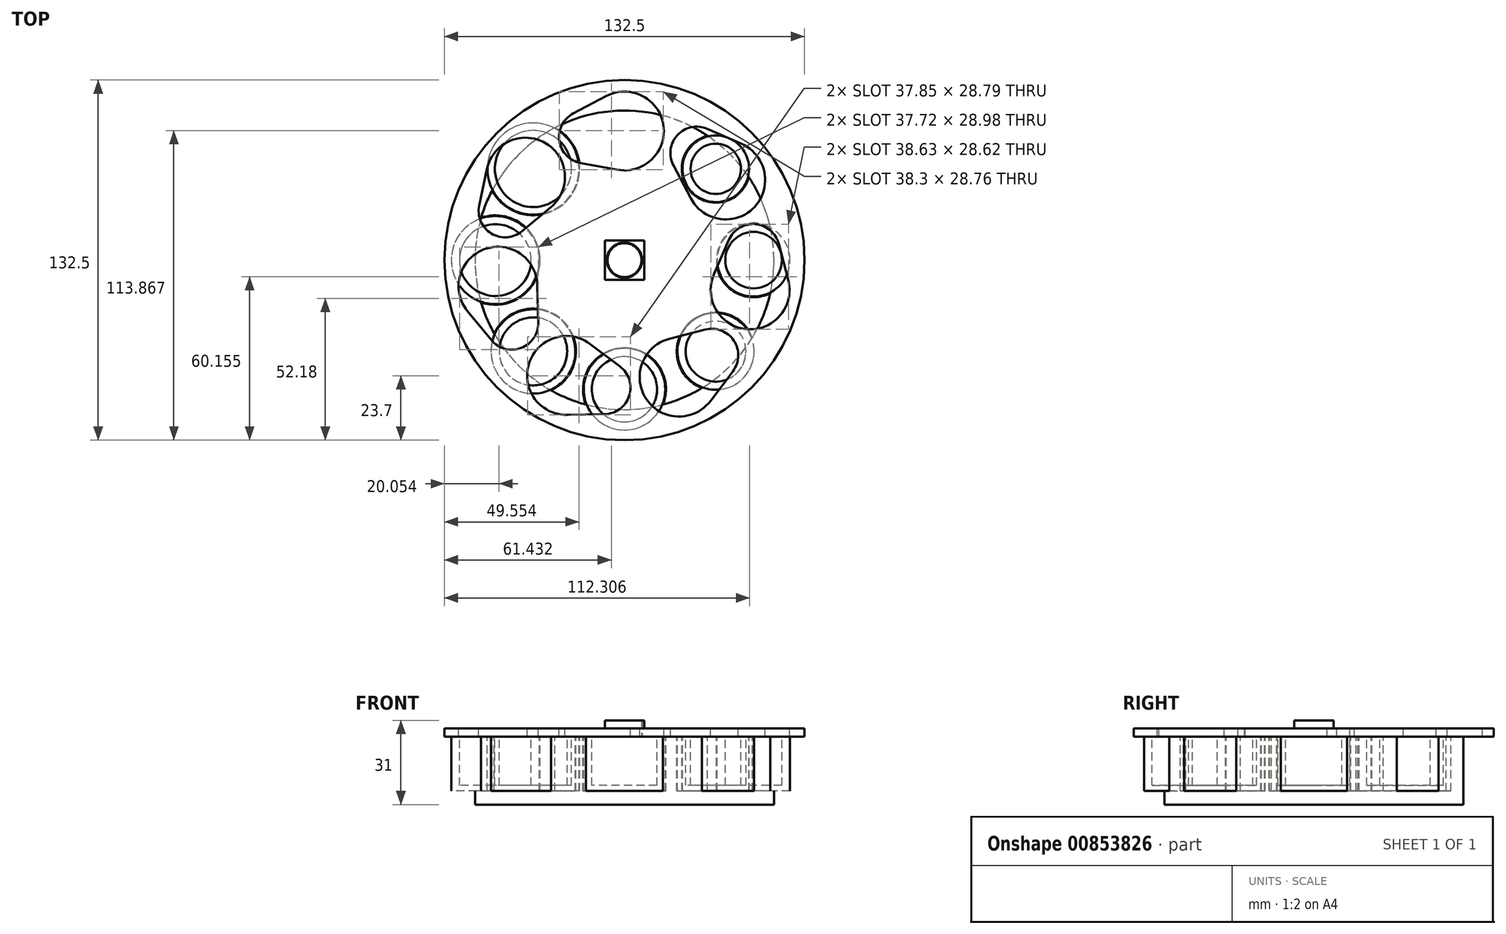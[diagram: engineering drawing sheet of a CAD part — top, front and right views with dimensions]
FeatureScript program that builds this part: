
annotation { "Feature Type Name" : "Feature", "Feature Type Description" : "" }
export const myFeature = defineFeature(function(context is Context, id is Id, definition is map)
    precondition{}
    {
        {
            var Q0;
            Q0=qCreatedBy(makeId("Top.planeOp"),FACE);
            var sketch = newSketch(context, id + "F0", { "sketchPlane" : qUnion([Q0])});
            skCircle(sketch, "E0", {"center": v(0, 0) * mm, "radius": 55 * mm});
            skCircle(sketch, "E1", {"center": v(0, 0) * mm, "radius": 47.5 * mm, "construction": true});
            skLineSegment(sketch, "E2", {"start": v(0, 0) * mm, "end": v(0, 47.5) * mm});
            skLineSegment(sketch, "E3.1.0", {"start": v(0, 0) * mm, "end": v(33.59, 33.59) * mm, "construction": true});
            skLineSegment(sketch, "E3.2.0", {"start": v(0, 0) * mm, "end": v(47.5, 0) * mm, "construction": true});
            skLineSegment(sketch, "E3.3.0", {"start": v(0, 0) * mm, "end": v(33.59, -33.59) * mm, "construction": true});
            skLineSegment(sketch, "E3.4.0", {"start": v(0, 0) * mm, "end": v(0, -47.5) * mm, "construction": true});
            skLineSegment(sketch, "E3.5.0", {"start": v(0, 0) * mm, "end": v(-33.59, -33.59) * mm, "construction": true});
            skLineSegment(sketch, "E3.6.0", {"start": v(0, 0) * mm, "end": v(-47.5, 0) * mm, "construction": true});
            skLineSegment(sketch, "E3.7.0", {"start": v(0, 0) * mm, "end": v(-33.59, 33.59) * mm});
            skLineSegment(sketch, "E3.anchor1", {"start": v(0, 0) * mm, "end": v(0, 47.5) * mm, "construction": true});
            skLineSegment(sketch, "E3.anchor2", {"start": v(0, 0) * mm, "end": v(-33.59, 33.59) * mm, "construction": true});
            skCircle(sketch, "E4", {"center": v(33.59, 33.59) * mm, "radius": 9.25 * mm});
            skCircle(sketch, "E5", {"center": v(47.5, 0) * mm, "radius": 10.4 * mm});
            skCircle(sketch, "E6", {"center": v(33.59, -33.59) * mm, "radius": 11.1 * mm});
            skCircle(sketch, "E7", {"center": v(0, -47.5) * mm, "radius": 12 * mm});
            skCircle(sketch, "E8", {"center": v(-33.59, -33.59) * mm, "radius": 12.5 * mm});
            skCircle(sketch, "E9", {"center": v(-47.5, 0) * mm, "radius": 13.2 * mm});
            skCircle(sketch, "E10", {"center": v(-33.59, 33.59) * mm, "radius": 14.1 * mm});
            skCircle(sketch, "E11.0", {"center": v(33.59, 33.59) * mm, "radius": 12.25 * mm});
            skCircle(sketch, "E12.0", {"center": v(47.5, 0) * mm, "radius": 13.4 * mm});
            skCircle(sketch, "E13.0", {"center": v(33.59, -33.59) * mm, "radius": 14.1 * mm});
            skCircle(sketch, "E14.0", {"center": v(0, -47.5) * mm, "radius": 15 * mm});
            skCircle(sketch, "E15.0", {"center": v(-33.59, -33.59) * mm, "radius": 15.5 * mm});
            skArc(sketch, "E16.0", {"start": v(-48.7, 25.57) * mm, "mid": v(-21.5, 21.5) * mm, "end": v(-25.57, 48.7) * mm});
            skArc(sketch, "E17.0", {"start": v(30.57, 45.72) * mm, "mid": v(24.75, 24.75) * mm, "end": v(45.72, 30.57) * mm});
            skArc(sketch, "E18.0", {"start": v(53.63, 12.2) * mm, "mid": v(33.85, 0) * mm, "end": v(53.63, -12.2) * mm});
            skArc(sketch, "E19.0", {"start": v(47.02, -28.53) * mm, "mid": v(23.44, -23.44) * mm, "end": v(28.53, -47.02) * mm});
            skArc(sketch, "E20.0", {"start": v(14.17, -53.14) * mm, "mid": v(0, -32.25) * mm, "end": v(-14.17, -53.14) * mm});
            skArc(sketch, "E21.0", {"start": v(-27.02, -47.9) * mm, "mid": v(-22.45, -22.45) * mm, "end": v(-47.9, -27.02) * mm});
            skCircle(sketch, "E22.0", {"center": v(-33.59, 33.59) * mm, "radius": 16.85 * mm});
            skCircle(sketch, "E23.0", {"center": v(-47.5, 0) * mm, "radius": 16.2 * mm});
            skArc(sketch, "E24.0", {"start": v(-52.74, -15.6) * mm, "mid": v(-31.05, 0) * mm, "end": v(-52.74, 15.6) * mm});
            skSolve(sketch);
        }
        {
            var Q0;
            {var subQ0=sQuery(id+"F0.wireOp",EDGE,"E16.0");var subQ1=sQuery(id+"F0.wireOp",EDGE,"E0");var subQ2=makeQuery(id+"F0.imprint","INTERSECT",VERTEX,{"disambiguationData":[OD(1.0)],"derivedFrom":[subQ1,subQ0]});Q0=makeQuery(id+"F0.imprint","IMPRINT",FACE,{"disambiguationData":[TD([[makeQuery(id+"F0.imprint","IMPRINT",EDGE,{"disambiguationData":[TD([[subQ2,1.0]])],"derivedFrom":subQ1}),1.0]])]});}
            var Q1;
            {var subQ5=sQuery(id+"F0.wireOp",EDGE,"E17.0");var subQ6=sQuery(id+"F0.wireOp",EDGE,"E0");var subQ7=makeQuery(id+"F0.imprint","INTERSECT",VERTEX,{"disambiguationData":[OD(1.0)],"derivedFrom":[subQ6,subQ5]});Q1=makeQuery(id+"F0.imprint","IMPRINT",FACE,{"disambiguationData":[TD([[makeQuery(id+"F0.imprint","IMPRINT",EDGE,{"disambiguationData":[TD([[subQ7,1.0]])],"derivedFrom":subQ6}),1.0]])]});}
            var Q2;
            {var subQ0=sQuery(id+"F0.wireOp",EDGE,"E18.0");var subQ1=sQuery(id+"F0.wireOp",EDGE,"E0");var subQ2=makeQuery(id+"F0.imprint","INTERSECT",VERTEX,{"disambiguationData":[OD(1.0)],"derivedFrom":[subQ1,subQ0]});Q2=makeQuery(id+"F0.imprint","IMPRINT",FACE,{"disambiguationData":[TD([[makeQuery(id+"F0.imprint","IMPRINT",EDGE,{"disambiguationData":[TD([[subQ2,1.0]])],"derivedFrom":subQ1}),1.0]])]});}
            var Q3;
            {var subQ0=sQuery(id+"F0.wireOp",EDGE,"E19.0");var subQ1=sQuery(id+"F0.wireOp",EDGE,"E0");var subQ2=makeQuery(id+"F0.imprint","INTERSECT",VERTEX,{"disambiguationData":[OD(1.0)],"derivedFrom":[subQ1,subQ0]});Q3=makeQuery(id+"F0.imprint","IMPRINT",FACE,{"disambiguationData":[TD([[makeQuery(id+"F0.imprint","IMPRINT",EDGE,{"disambiguationData":[TD([[subQ2,1.0]])],"derivedFrom":subQ1}),1.0]])]});}
            var Q4;
            {var subQ0=sQuery(id+"F0.wireOp",EDGE,"E20.0");var subQ1=sQuery(id+"F0.wireOp",EDGE,"E0");var subQ2=makeQuery(id+"F0.imprint","INTERSECT",VERTEX,{"disambiguationData":[OD(1.0)],"derivedFrom":[subQ1,subQ0]});Q4=makeQuery(id+"F0.imprint","IMPRINT",FACE,{"disambiguationData":[TD([[makeQuery(id+"F0.imprint","IMPRINT",EDGE,{"disambiguationData":[TD([[subQ2,1.0]])],"derivedFrom":subQ1}),1.0]])]});}
            var Q5;
            {var subQ5=sQuery(id+"F0.wireOp",EDGE,"E21.0");var subQ7=sQuery(id+"F0.wireOp",EDGE,"E0");var subQ8=makeQuery(id+"F0.imprint","INTERSECT",VERTEX,{"disambiguationData":[OD(1.0)],"derivedFrom":[subQ7,subQ5]});Q5=makeQuery(id+"F0.imprint","IMPRINT",FACE,{"disambiguationData":[TD([[makeQuery(id+"F0.imprint","IMPRINT",EDGE,{"disambiguationData":[TD([[subQ8,1.0]])],"derivedFrom":subQ7}),1.0]])]});}
            var Q6;
            {var subQ3=sQuery(id+"F0.wireOp",EDGE,"E16.0");var subQ7=sQuery(id+"F0.wireOp",EDGE,"E0");var subQ8=makeQuery(id+"F0.imprint","INTERSECT",VERTEX,{"disambiguationData":[OD(0.0)],"derivedFrom":[subQ7,subQ3]});Q6=makeQuery(id+"F0.imprint","IMPRINT",FACE,{"disambiguationData":[TD([[makeQuery(id+"F0.imprint","IMPRINT",EDGE,{"disambiguationData":[TD([[subQ8,-1.0]])],"derivedFrom":subQ7}),1.0]])]});}
            extrude(context, id + "F1", {"entities" : qUnion([Q0, Q1, Q2, Q3, Q4, Q5, Q6]), "oppositeDirection" : true, "depth" : 20 * mm, "offsetDistance" : 25 * mm});
        }
        {
            var Q0;
            {var subQ0=sQuery(id+"F0.wireOp",EDGE,"E16.0");var subQ1=sQuery(id+"F0.wireOp",EDGE,"E0");var subQ2=makeQuery(id+"F0.imprint","INTERSECT",VERTEX,{"disambiguationData":[OD(1.0)],"derivedFrom":[subQ1,subQ0]});Q0=makeQuery(id+"F0.imprint","IMPRINT",FACE,{"disambiguationData":[TD([[makeQuery(id+"F0.imprint","IMPRINT",EDGE,{"disambiguationData":[TD([[subQ2,1.0]])],"derivedFrom":subQ1}),1.0]])]});}
            var Q1;
            {var subQ5=sQuery(id+"F0.wireOp",EDGE,"E17.0");var subQ6=sQuery(id+"F0.wireOp",EDGE,"E0");var subQ7=makeQuery(id+"F0.imprint","INTERSECT",VERTEX,{"disambiguationData":[OD(1.0)],"derivedFrom":[subQ6,subQ5]});Q1=makeQuery(id+"F0.imprint","IMPRINT",FACE,{"disambiguationData":[TD([[makeQuery(id+"F0.imprint","IMPRINT",EDGE,{"disambiguationData":[TD([[subQ7,1.0]])],"derivedFrom":subQ6}),1.0]])]});}
            var Q2;
            {var subQ0=sQuery(id+"F0.wireOp",EDGE,"E18.0");var subQ1=sQuery(id+"F0.wireOp",EDGE,"E0");var subQ2=makeQuery(id+"F0.imprint","INTERSECT",VERTEX,{"disambiguationData":[OD(1.0)],"derivedFrom":[subQ1,subQ0]});Q2=makeQuery(id+"F0.imprint","IMPRINT",FACE,{"disambiguationData":[TD([[makeQuery(id+"F0.imprint","IMPRINT",EDGE,{"disambiguationData":[TD([[subQ2,1.0]])],"derivedFrom":subQ1}),1.0]])]});}
            var Q3;
            {var subQ0=sQuery(id+"F0.wireOp",EDGE,"E19.0");var subQ1=sQuery(id+"F0.wireOp",EDGE,"E0");var subQ2=makeQuery(id+"F0.imprint","INTERSECT",VERTEX,{"disambiguationData":[OD(1.0)],"derivedFrom":[subQ1,subQ0]});Q3=makeQuery(id+"F0.imprint","IMPRINT",FACE,{"disambiguationData":[TD([[makeQuery(id+"F0.imprint","IMPRINT",EDGE,{"disambiguationData":[TD([[subQ2,1.0]])],"derivedFrom":subQ1}),1.0]])]});}
            var Q4;
            {var subQ0=sQuery(id+"F0.wireOp",EDGE,"E20.0");var subQ1=sQuery(id+"F0.wireOp",EDGE,"E0");var subQ2=makeQuery(id+"F0.imprint","INTERSECT",VERTEX,{"disambiguationData":[OD(1.0)],"derivedFrom":[subQ1,subQ0]});Q4=makeQuery(id+"F0.imprint","IMPRINT",FACE,{"disambiguationData":[TD([[makeQuery(id+"F0.imprint","IMPRINT",EDGE,{"disambiguationData":[TD([[subQ2,1.0]])],"derivedFrom":subQ1}),1.0]])]});}
            var Q5;
            {var subQ5=sQuery(id+"F0.wireOp",EDGE,"E21.0");var subQ7=sQuery(id+"F0.wireOp",EDGE,"E0");var subQ8=makeQuery(id+"F0.imprint","INTERSECT",VERTEX,{"disambiguationData":[OD(1.0)],"derivedFrom":[subQ7,subQ5]});Q5=makeQuery(id+"F0.imprint","IMPRINT",FACE,{"disambiguationData":[TD([[makeQuery(id+"F0.imprint","IMPRINT",EDGE,{"disambiguationData":[TD([[subQ8,1.0]])],"derivedFrom":subQ7}),1.0]])]});}
            var Q6;
            {var subQ3=sQuery(id+"F0.wireOp",EDGE,"E16.0");var subQ7=sQuery(id+"F0.wireOp",EDGE,"E0");var subQ8=makeQuery(id+"F0.imprint","INTERSECT",VERTEX,{"disambiguationData":[OD(0.0)],"derivedFrom":[subQ7,subQ3]});Q6=makeQuery(id+"F0.imprint","IMPRINT",FACE,{"disambiguationData":[TD([[makeQuery(id+"F0.imprint","IMPRINT",EDGE,{"disambiguationData":[TD([[subQ8,-1.0]])],"derivedFrom":subQ7}),1.0]])]});}
            var Q7;
            {var subQ0=sQuery(id+"F0.wireOp",EDGE,"E22.0");var subQ1=sQuery(id+"F0.wireOp",EDGE,"E0");var subQ2=makeQuery(id+"F0.imprint","INTERSECT",VERTEX,{"disambiguationData":[OD(1.0)],"derivedFrom":[subQ1,subQ0]});Q7=makeQuery(id+"F0.imprint","IMPRINT",FACE,{"disambiguationData":[TD([[makeQuery(id+"F0.imprint","IMPRINT",EDGE,{"disambiguationData":[TD([[subQ2,1.0]])],"derivedFrom":subQ1}),1.0]])]});}
            var Q8;
            {var subQ0=sQuery(id+"F0.wireOp",EDGE,"E10");var subQ1=sQuery(id+"F0.wireOp",EDGE,"E0");var subQ2=makeQuery(id+"F0.imprint","INTERSECT",VERTEX,{"disambiguationData":[OD(0.0)],"derivedFrom":[subQ1,subQ0]});Q8=makeQuery(id+"F0.imprint","IMPRINT",FACE,{"disambiguationData":[TD([[makeQuery(id+"F0.imprint","IMPRINT",EDGE,{"disambiguationData":[TD([[subQ2,-1.0]])],"derivedFrom":subQ1}),1.0]])]});}
            var Q9;
            {var subQ0=sQuery(id+"F0.wireOp",EDGE,"E22.0");var subQ1=sQuery(id+"F0.wireOp",EDGE,"E0");var subQ2=makeQuery(id+"F0.imprint","INTERSECT",VERTEX,{"disambiguationData":[OD(0.0)],"derivedFrom":[subQ1,subQ0]});Q9=makeQuery(id+"F0.imprint","IMPRINT",FACE,{"disambiguationData":[TD([[makeQuery(id+"F0.imprint","IMPRINT",EDGE,{"disambiguationData":[TD([[subQ2,-1.0]])],"derivedFrom":subQ1}),1.0]])]});}
            var Q10;
            {var subQ0=sQuery(id+"F0.wireOp",EDGE,"E11.0");var subQ1=sQuery(id+"F0.wireOp",EDGE,"E0");var subQ2=makeQuery(id+"F0.imprint","INTERSECT",VERTEX,{"disambiguationData":[OD(1.0)],"derivedFrom":[subQ1,subQ0]});Q10=makeQuery(id+"F0.imprint","IMPRINT",FACE,{"disambiguationData":[TD([[makeQuery(id+"F0.imprint","IMPRINT",EDGE,{"disambiguationData":[TD([[subQ2,1.0]])],"derivedFrom":subQ1}),1.0]])]});}
            var Q11;
            {var subQ0=sQuery(id+"F0.wireOp",EDGE,"E4");var subQ1=sQuery(id+"F0.wireOp",EDGE,"E0");var subQ2=makeQuery(id+"F0.imprint","INTERSECT",VERTEX,{"disambiguationData":[OD(0.0)],"derivedFrom":[subQ1,subQ0]});Q11=makeQuery(id+"F0.imprint","IMPRINT",FACE,{"disambiguationData":[TD([[makeQuery(id+"F0.imprint","IMPRINT",EDGE,{"disambiguationData":[TD([[subQ2,-1.0]])],"derivedFrom":subQ1}),1.0]])]});}
            var Q12;
            {var subQ0=sQuery(id+"F0.wireOp",EDGE,"E11.0");var subQ1=sQuery(id+"F0.wireOp",EDGE,"E0");var subQ2=makeQuery(id+"F0.imprint","INTERSECT",VERTEX,{"disambiguationData":[OD(0.0)],"derivedFrom":[subQ1,subQ0]});Q12=makeQuery(id+"F0.imprint","IMPRINT",FACE,{"disambiguationData":[TD([[makeQuery(id+"F0.imprint","IMPRINT",EDGE,{"disambiguationData":[TD([[subQ2,-1.0]])],"derivedFrom":subQ1}),1.0]])]});}
            var Q13;
            {var subQ0=sQuery(id+"F0.wireOp",EDGE,"E12.0");var subQ1=sQuery(id+"F0.wireOp",EDGE,"E0");var subQ2=makeQuery(id+"F0.imprint","INTERSECT",VERTEX,{"disambiguationData":[OD(0.0)],"derivedFrom":[subQ1,subQ0]});Q13=makeQuery(id+"F0.imprint","IMPRINT",FACE,{"disambiguationData":[TD([[makeQuery(id+"F0.imprint","IMPRINT",EDGE,{"disambiguationData":[TD([[subQ2,1.0]])],"derivedFrom":subQ1}),1.0]])]});}
            var Q14;
            {var subQ0=sQuery(id+"F0.wireOp",EDGE,"E5");var subQ1=sQuery(id+"F0.wireOp",EDGE,"E0");var subQ2=makeQuery(id+"F0.imprint","INTERSECT",VERTEX,{"disambiguationData":[OD(0.0)],"derivedFrom":[subQ1,subQ0]});Q14=makeQuery(id+"F0.imprint","IMPRINT",FACE,{"disambiguationData":[TD([[makeQuery(id+"F0.imprint","IMPRINT",EDGE,{"disambiguationData":[TD([[subQ2,1.0]])],"derivedFrom":subQ1}),1.0]])]});}
            var Q15;
            {var subQ0=sQuery(id+"F0.wireOp",EDGE,"E12.0");var subQ1=sQuery(id+"F0.wireOp",EDGE,"E0");var subQ2=makeQuery(id+"F0.imprint","INTERSECT",VERTEX,{"disambiguationData":[OD(1.0)],"derivedFrom":[subQ1,subQ0]});Q15=makeQuery(id+"F0.imprint","IMPRINT",FACE,{"disambiguationData":[TD([[makeQuery(id+"F0.imprint","IMPRINT",EDGE,{"disambiguationData":[TD([[subQ2,-1.0]])],"derivedFrom":subQ1}),1.0]])]});}
            var Q16;
            {var subQ0=sQuery(id+"F0.wireOp",EDGE,"E13.0");var subQ1=sQuery(id+"F0.wireOp",EDGE,"E0");var subQ2=makeQuery(id+"F0.imprint","INTERSECT",VERTEX,{"disambiguationData":[OD(1.0)],"derivedFrom":[subQ1,subQ0]});Q16=makeQuery(id+"F0.imprint","IMPRINT",FACE,{"disambiguationData":[TD([[makeQuery(id+"F0.imprint","IMPRINT",EDGE,{"disambiguationData":[TD([[subQ2,1.0]])],"derivedFrom":subQ1}),1.0]])]});}
            var Q17;
            {var subQ0=sQuery(id+"F0.wireOp",EDGE,"E6");var subQ1=sQuery(id+"F0.wireOp",EDGE,"E0");var subQ2=makeQuery(id+"F0.imprint","INTERSECT",VERTEX,{"disambiguationData":[OD(0.0)],"derivedFrom":[subQ1,subQ0]});Q17=makeQuery(id+"F0.imprint","IMPRINT",FACE,{"disambiguationData":[TD([[makeQuery(id+"F0.imprint","IMPRINT",EDGE,{"disambiguationData":[TD([[subQ2,-1.0]])],"derivedFrom":subQ1}),1.0]])]});}
            var Q18;
            {var subQ0=sQuery(id+"F0.wireOp",EDGE,"E13.0");var subQ1=sQuery(id+"F0.wireOp",EDGE,"E0");var subQ2=makeQuery(id+"F0.imprint","INTERSECT",VERTEX,{"disambiguationData":[OD(0.0)],"derivedFrom":[subQ1,subQ0]});Q18=makeQuery(id+"F0.imprint","IMPRINT",FACE,{"disambiguationData":[TD([[makeQuery(id+"F0.imprint","IMPRINT",EDGE,{"disambiguationData":[TD([[subQ2,-1.0]])],"derivedFrom":subQ1}),1.0]])]});}
            var Q19;
            {var subQ0=sQuery(id+"F0.wireOp",EDGE,"E14.0");var subQ1=sQuery(id+"F0.wireOp",EDGE,"E0");var subQ2=makeQuery(id+"F0.imprint","INTERSECT",VERTEX,{"disambiguationData":[OD(1.0)],"derivedFrom":[subQ1,subQ0]});Q19=makeQuery(id+"F0.imprint","IMPRINT",FACE,{"disambiguationData":[TD([[makeQuery(id+"F0.imprint","IMPRINT",EDGE,{"disambiguationData":[TD([[subQ2,1.0]])],"derivedFrom":subQ1}),1.0]])]});}
            var Q20;
            {var subQ0=sQuery(id+"F0.wireOp",EDGE,"E7");var subQ1=sQuery(id+"F0.wireOp",EDGE,"E0");var subQ2=makeQuery(id+"F0.imprint","INTERSECT",VERTEX,{"disambiguationData":[OD(0.0)],"derivedFrom":[subQ1,subQ0]});Q20=makeQuery(id+"F0.imprint","IMPRINT",FACE,{"disambiguationData":[TD([[makeQuery(id+"F0.imprint","IMPRINT",EDGE,{"disambiguationData":[TD([[subQ2,-1.0]])],"derivedFrom":subQ1}),1.0]])]});}
            var Q21;
            {var subQ0=sQuery(id+"F0.wireOp",EDGE,"E14.0");var subQ1=sQuery(id+"F0.wireOp",EDGE,"E0");var subQ2=makeQuery(id+"F0.imprint","INTERSECT",VERTEX,{"disambiguationData":[OD(0.0)],"derivedFrom":[subQ1,subQ0]});Q21=makeQuery(id+"F0.imprint","IMPRINT",FACE,{"disambiguationData":[TD([[makeQuery(id+"F0.imprint","IMPRINT",EDGE,{"disambiguationData":[TD([[subQ2,-1.0]])],"derivedFrom":subQ1}),1.0]])]});}
            var Q22;
            {var subQ0=sQuery(id+"F0.wireOp",EDGE,"E15.0");var subQ1=sQuery(id+"F0.wireOp",EDGE,"E0");var subQ2=makeQuery(id+"F0.imprint","INTERSECT",VERTEX,{"disambiguationData":[OD(1.0)],"derivedFrom":[subQ1,subQ0]});Q22=makeQuery(id+"F0.imprint","IMPRINT",FACE,{"disambiguationData":[TD([[makeQuery(id+"F0.imprint","IMPRINT",EDGE,{"disambiguationData":[TD([[subQ2,1.0]])],"derivedFrom":subQ1}),1.0]])]});}
            var Q23;
            {var subQ0=sQuery(id+"F0.wireOp",EDGE,"E8");var subQ1=sQuery(id+"F0.wireOp",EDGE,"E0");var subQ2=makeQuery(id+"F0.imprint","INTERSECT",VERTEX,{"disambiguationData":[OD(0.0)],"derivedFrom":[subQ1,subQ0]});Q23=makeQuery(id+"F0.imprint","IMPRINT",FACE,{"disambiguationData":[TD([[makeQuery(id+"F0.imprint","IMPRINT",EDGE,{"disambiguationData":[TD([[subQ2,-1.0]])],"derivedFrom":subQ1}),1.0]])]});}
            var Q24;
            {var subQ0=sQuery(id+"F0.wireOp",EDGE,"E15.0");var subQ1=sQuery(id+"F0.wireOp",EDGE,"E0");var subQ2=makeQuery(id+"F0.imprint","INTERSECT",VERTEX,{"disambiguationData":[OD(0.0)],"derivedFrom":[subQ1,subQ0]});Q24=makeQuery(id+"F0.imprint","IMPRINT",FACE,{"disambiguationData":[TD([[makeQuery(id+"F0.imprint","IMPRINT",EDGE,{"disambiguationData":[TD([[subQ2,-1.0]])],"derivedFrom":subQ1}),1.0]])]});}
            var Q25;
            {var subQ0=sQuery(id+"F0.wireOp",EDGE,"E23.0");var subQ1=sQuery(id+"F0.wireOp",EDGE,"E0");var subQ2=makeQuery(id+"F0.imprint","INTERSECT",VERTEX,{"disambiguationData":[OD(1.0)],"derivedFrom":[subQ1,subQ0]});Q25=makeQuery(id+"F0.imprint","IMPRINT",FACE,{"disambiguationData":[TD([[makeQuery(id+"F0.imprint","IMPRINT",EDGE,{"disambiguationData":[TD([[subQ2,1.0]])],"derivedFrom":subQ1}),1.0]])]});}
            var Q26;
            {var subQ0=sQuery(id+"F0.wireOp",EDGE,"E9");var subQ1=sQuery(id+"F0.wireOp",EDGE,"E0");var subQ2=makeQuery(id+"F0.imprint","INTERSECT",VERTEX,{"disambiguationData":[OD(0.0)],"derivedFrom":[subQ1,subQ0]});Q26=makeQuery(id+"F0.imprint","IMPRINT",FACE,{"disambiguationData":[TD([[makeQuery(id+"F0.imprint","IMPRINT",EDGE,{"disambiguationData":[TD([[subQ2,-1.0]])],"derivedFrom":subQ1}),1.0]])]});}
            var Q27;
            {var subQ0=sQuery(id+"F0.wireOp",EDGE,"E23.0");var subQ1=sQuery(id+"F0.wireOp",EDGE,"E0");var subQ2=makeQuery(id+"F0.imprint","INTERSECT",VERTEX,{"disambiguationData":[OD(0.0)],"derivedFrom":[subQ1,subQ0]});Q27=makeQuery(id+"F0.imprint","IMPRINT",FACE,{"disambiguationData":[TD([[makeQuery(id+"F0.imprint","IMPRINT",EDGE,{"disambiguationData":[TD([[subQ2,-1.0]])],"derivedFrom":subQ1}),1.0]])]});}
            var Q28;
            {var subQ0=sQuery(id+"F0.wireOp",EDGE,"E16.0");var subQ1=sQuery(id+"F0.wireOp",EDGE,"E0");var subQ2=makeQuery(id+"F0.imprint","INTERSECT",VERTEX,{"disambiguationData":[OD(0.0)],"derivedFrom":[subQ1,subQ0]});Q28=makeQuery(id+"F0.imprint","IMPRINT",FACE,{"disambiguationData":[TD([[makeQuery(id+"F0.imprint","IMPRINT",EDGE,{"disambiguationData":[TD([[subQ2,1.0]])],"derivedFrom":subQ1}),1.0]])]});}
            var Q29;
            {var subQ0=sQuery(id+"F0.wireOp",EDGE,"E16.0");var subQ1=sQuery(id+"F0.wireOp",EDGE,"E0");var subQ2=makeQuery(id+"F0.imprint","INTERSECT",VERTEX,{"disambiguationData":[OD(1.0)],"derivedFrom":[subQ1,subQ0]});Q29=makeQuery(id+"F0.imprint","IMPRINT",FACE,{"disambiguationData":[TD([[makeQuery(id+"F0.imprint","IMPRINT",EDGE,{"disambiguationData":[TD([[subQ2,-1.0]])],"derivedFrom":subQ1}),1.0]])]});}
            var Q30;
            {var subQ0=sQuery(id+"F0.wireOp",EDGE,"E17.0");var subQ1=sQuery(id+"F0.wireOp",EDGE,"E0");var subQ2=makeQuery(id+"F0.imprint","INTERSECT",VERTEX,{"disambiguationData":[OD(1.0)],"derivedFrom":[subQ1,subQ0]});Q30=makeQuery(id+"F0.imprint","IMPRINT",FACE,{"disambiguationData":[TD([[makeQuery(id+"F0.imprint","IMPRINT",EDGE,{"disambiguationData":[TD([[subQ2,-1.0]])],"derivedFrom":subQ1}),1.0]])]});}
            var Q31;
            {var subQ0=sQuery(id+"F0.wireOp",EDGE,"E17.0");var subQ1=sQuery(id+"F0.wireOp",EDGE,"E0");var subQ2=makeQuery(id+"F0.imprint","INTERSECT",VERTEX,{"disambiguationData":[OD(0.0)],"derivedFrom":[subQ1,subQ0]});Q31=makeQuery(id+"F0.imprint","IMPRINT",FACE,{"disambiguationData":[TD([[makeQuery(id+"F0.imprint","IMPRINT",EDGE,{"disambiguationData":[TD([[subQ2,1.0]])],"derivedFrom":subQ1}),1.0]])]});}
            var Q32;
            {var subQ0=sQuery(id+"F0.wireOp",EDGE,"E18.0");var subQ1=sQuery(id+"F0.wireOp",EDGE,"E0");var subQ2=makeQuery(id+"F0.imprint","INTERSECT",VERTEX,{"disambiguationData":[OD(0.0)],"derivedFrom":[subQ1,subQ0]});Q32=makeQuery(id+"F0.imprint","IMPRINT",FACE,{"disambiguationData":[TD([[makeQuery(id+"F0.imprint","IMPRINT",EDGE,{"disambiguationData":[TD([[subQ2,1.0]])],"derivedFrom":subQ1}),1.0]])]});}
            var Q33;
            {var subQ0=sQuery(id+"F0.wireOp",EDGE,"E18.0");var subQ1=sQuery(id+"F0.wireOp",EDGE,"E0");var subQ2=makeQuery(id+"F0.imprint","INTERSECT",VERTEX,{"disambiguationData":[OD(1.0)],"derivedFrom":[subQ1,subQ0]});Q33=makeQuery(id+"F0.imprint","IMPRINT",FACE,{"disambiguationData":[TD([[makeQuery(id+"F0.imprint","IMPRINT",EDGE,{"disambiguationData":[TD([[subQ2,-1.0]])],"derivedFrom":subQ1}),1.0]])]});}
            var Q34;
            {var subQ0=sQuery(id+"F0.wireOp",EDGE,"E19.0");var subQ1=sQuery(id+"F0.wireOp",EDGE,"E0");var subQ2=makeQuery(id+"F0.imprint","INTERSECT",VERTEX,{"disambiguationData":[OD(0.0)],"derivedFrom":[subQ1,subQ0]});Q34=makeQuery(id+"F0.imprint","IMPRINT",FACE,{"disambiguationData":[TD([[makeQuery(id+"F0.imprint","IMPRINT",EDGE,{"disambiguationData":[TD([[subQ2,1.0]])],"derivedFrom":subQ1}),1.0]])]});}
            var Q35;
            {var subQ0=sQuery(id+"F0.wireOp",EDGE,"E19.0");var subQ1=sQuery(id+"F0.wireOp",EDGE,"E0");var subQ2=makeQuery(id+"F0.imprint","INTERSECT",VERTEX,{"disambiguationData":[OD(1.0)],"derivedFrom":[subQ1,subQ0]});Q35=makeQuery(id+"F0.imprint","IMPRINT",FACE,{"disambiguationData":[TD([[makeQuery(id+"F0.imprint","IMPRINT",EDGE,{"disambiguationData":[TD([[subQ2,-1.0]])],"derivedFrom":subQ1}),1.0]])]});}
            var Q36;
            {var subQ0=sQuery(id+"F0.wireOp",EDGE,"E20.0");var subQ1=sQuery(id+"F0.wireOp",EDGE,"E0");var subQ2=makeQuery(id+"F0.imprint","INTERSECT",VERTEX,{"disambiguationData":[OD(0.0)],"derivedFrom":[subQ1,subQ0]});Q36=makeQuery(id+"F0.imprint","IMPRINT",FACE,{"disambiguationData":[TD([[makeQuery(id+"F0.imprint","IMPRINT",EDGE,{"disambiguationData":[TD([[subQ2,1.0]])],"derivedFrom":subQ1}),1.0]])]});}
            var Q37;
            {var subQ0=sQuery(id+"F0.wireOp",EDGE,"E20.0");var subQ1=sQuery(id+"F0.wireOp",EDGE,"E0");var subQ2=makeQuery(id+"F0.imprint","INTERSECT",VERTEX,{"disambiguationData":[OD(1.0)],"derivedFrom":[subQ1,subQ0]});Q37=makeQuery(id+"F0.imprint","IMPRINT",FACE,{"disambiguationData":[TD([[makeQuery(id+"F0.imprint","IMPRINT",EDGE,{"disambiguationData":[TD([[subQ2,-1.0]])],"derivedFrom":subQ1}),1.0]])]});}
            var Q38;
            {var subQ0=sQuery(id+"F0.wireOp",EDGE,"E21.0");var subQ1=sQuery(id+"F0.wireOp",EDGE,"E0");var subQ2=makeQuery(id+"F0.imprint","INTERSECT",VERTEX,{"disambiguationData":[OD(0.0)],"derivedFrom":[subQ1,subQ0]});Q38=makeQuery(id+"F0.imprint","IMPRINT",FACE,{"disambiguationData":[TD([[makeQuery(id+"F0.imprint","IMPRINT",EDGE,{"disambiguationData":[TD([[subQ2,1.0]])],"derivedFrom":subQ1}),1.0]])]});}
            var Q39;
            {var subQ0=sQuery(id+"F0.wireOp",EDGE,"E21.0");var subQ1=sQuery(id+"F0.wireOp",EDGE,"E0");var subQ2=makeQuery(id+"F0.imprint","INTERSECT",VERTEX,{"disambiguationData":[OD(1.0)],"derivedFrom":[subQ1,subQ0]});Q39=makeQuery(id+"F0.imprint","IMPRINT",FACE,{"disambiguationData":[TD([[makeQuery(id+"F0.imprint","IMPRINT",EDGE,{"disambiguationData":[TD([[subQ2,-1.0]])],"derivedFrom":subQ1}),1.0]])]});}
            var Q40;
            {var subQ0=sQuery(id+"F0.wireOp",EDGE,"E24.0");var subQ1=sQuery(id+"F0.wireOp",EDGE,"E0");var subQ2=makeQuery(id+"F0.imprint","INTERSECT",VERTEX,{"disambiguationData":[OD(0.0)],"derivedFrom":[subQ1,subQ0]});Q40=makeQuery(id+"F0.imprint","IMPRINT",FACE,{"disambiguationData":[TD([[makeQuery(id+"F0.imprint","IMPRINT",EDGE,{"disambiguationData":[TD([[subQ2,1.0]])],"derivedFrom":subQ1}),1.0]])]});}
            var Q41;
            {var subQ0=sQuery(id+"F0.wireOp",EDGE,"E24.0");var subQ1=sQuery(id+"F0.wireOp",EDGE,"E0");var subQ2=makeQuery(id+"F0.imprint","INTERSECT",VERTEX,{"disambiguationData":[OD(1.0)],"derivedFrom":[subQ1,subQ0]});Q41=makeQuery(id+"F0.imprint","IMPRINT",FACE,{"disambiguationData":[TD([[makeQuery(id+"F0.imprint","IMPRINT",EDGE,{"disambiguationData":[TD([[subQ2,-1.0]])],"derivedFrom":subQ1}),1.0]])]});}
            extrude(context, id + "F2", {"entities" : qUnion([Q0, Q1, Q2, Q3, Q4, Q5, Q6, Q7, Q8, Q9, Q10, Q11, Q12, Q13, Q14, Q15, Q16, Q17, Q18, Q19, Q20, Q21, Q22, Q23, Q24, Q25, Q26, Q27, Q28, Q29, Q30, Q31, Q32, Q33, Q34, Q35, Q36, Q37, Q38, Q39, Q40, Q41]), "operationType" : NewBodyOperationType.ADD, "oppositeDirection" : true, "depth" : 25 * mm, "offsetDistance" : 25 * mm, "hasSecondDirection" : true, "secondDirectionOppositeDirection" : true, "secondDirectionDepth" : 20 * mm});
        }
        {
            var Q0;
            {var subQ0=sQuery(id+"F0.wireOp",EDGE,"E15.0");var subQ1=sQuery(id+"F0.wireOp",EDGE,"E0");var subQ2=makeQuery(id+"F0.imprint","INTERSECT",VERTEX,{"disambiguationData":[OD(0.0)],"derivedFrom":[subQ1,subQ0]});Q0=makeQuery(id+"F0.imprint","IMPRINT",FACE,{"disambiguationData":[TD([[makeQuery(id+"F0.imprint","IMPRINT",EDGE,{"disambiguationData":[TD([[subQ2,-1.0]])],"derivedFrom":subQ1}),-1.0]])]});}
            var Q1;
            {var subQ0=sQuery(id+"F0.wireOp",EDGE,"E8");var subQ1=sQuery(id+"F0.wireOp",EDGE,"E0");var subQ2=makeQuery(id+"F0.imprint","INTERSECT",VERTEX,{"disambiguationData":[OD(0.0)],"derivedFrom":[subQ1,subQ0]});Q1=makeQuery(id+"F0.imprint","IMPRINT",FACE,{"disambiguationData":[TD([[makeQuery(id+"F0.imprint","IMPRINT",EDGE,{"disambiguationData":[TD([[subQ2,-1.0]])],"derivedFrom":subQ1}),-1.0]])]});}
            var Q2;
            {var subQ0=sQuery(id+"F0.wireOp",EDGE,"E8");var subQ1=sQuery(id+"F0.wireOp",EDGE,"E0");var subQ2=makeQuery(id+"F0.imprint","INTERSECT",VERTEX,{"disambiguationData":[OD(0.0)],"derivedFrom":[subQ1,subQ0]});Q2=makeQuery(id+"F0.imprint","IMPRINT",FACE,{"disambiguationData":[TD([[makeQuery(id+"F0.imprint","IMPRINT",EDGE,{"disambiguationData":[TD([[subQ2,-1.0]])],"derivedFrom":subQ1}),1.0]])]});}
            var Q3;
            {var subQ0=sQuery(id+"F0.wireOp",EDGE,"E15.0");var subQ1=sQuery(id+"F0.wireOp",EDGE,"E0");var subQ2=makeQuery(id+"F0.imprint","INTERSECT",VERTEX,{"disambiguationData":[OD(0.0)],"derivedFrom":[subQ1,subQ0]});Q3=makeQuery(id+"F0.imprint","IMPRINT",FACE,{"disambiguationData":[TD([[makeQuery(id+"F0.imprint","IMPRINT",EDGE,{"disambiguationData":[TD([[subQ2,-1.0]])],"derivedFrom":subQ1}),1.0]])]});}
            var Q4;
            {var subQ0=sQuery(id+"F0.wireOp",EDGE,"E14.0");var subQ1=sQuery(id+"F0.wireOp",EDGE,"E0");var subQ2=makeQuery(id+"F0.imprint","INTERSECT",VERTEX,{"disambiguationData":[OD(0.0)],"derivedFrom":[subQ1,subQ0]});Q4=makeQuery(id+"F0.imprint","IMPRINT",FACE,{"disambiguationData":[TD([[makeQuery(id+"F0.imprint","IMPRINT",EDGE,{"disambiguationData":[TD([[subQ2,-1.0]])],"derivedFrom":subQ1}),-1.0]])]});}
            var Q5;
            {var subQ0=sQuery(id+"F0.wireOp",EDGE,"E7");var subQ1=sQuery(id+"F0.wireOp",EDGE,"E0");var subQ2=makeQuery(id+"F0.imprint","INTERSECT",VERTEX,{"disambiguationData":[OD(0.0)],"derivedFrom":[subQ1,subQ0]});Q5=makeQuery(id+"F0.imprint","IMPRINT",FACE,{"disambiguationData":[TD([[makeQuery(id+"F0.imprint","IMPRINT",EDGE,{"disambiguationData":[TD([[subQ2,-1.0]])],"derivedFrom":subQ1}),-1.0]])]});}
            var Q6;
            {var subQ0=sQuery(id+"F0.wireOp",EDGE,"E7");var subQ1=sQuery(id+"F0.wireOp",EDGE,"E0");var subQ2=makeQuery(id+"F0.imprint","INTERSECT",VERTEX,{"disambiguationData":[OD(0.0)],"derivedFrom":[subQ1,subQ0]});Q6=makeQuery(id+"F0.imprint","IMPRINT",FACE,{"disambiguationData":[TD([[makeQuery(id+"F0.imprint","IMPRINT",EDGE,{"disambiguationData":[TD([[subQ2,-1.0]])],"derivedFrom":subQ1}),1.0]])]});}
            var Q7;
            {var subQ0=sQuery(id+"F0.wireOp",EDGE,"E14.0");var subQ1=sQuery(id+"F0.wireOp",EDGE,"E0");var subQ2=makeQuery(id+"F0.imprint","INTERSECT",VERTEX,{"disambiguationData":[OD(0.0)],"derivedFrom":[subQ1,subQ0]});Q7=makeQuery(id+"F0.imprint","IMPRINT",FACE,{"disambiguationData":[TD([[makeQuery(id+"F0.imprint","IMPRINT",EDGE,{"disambiguationData":[TD([[subQ2,-1.0]])],"derivedFrom":subQ1}),1.0]])]});}
            var Q8;
            {var subQ0=sQuery(id+"F0.wireOp",EDGE,"E23.0");var subQ1=sQuery(id+"F0.wireOp",EDGE,"E0");var subQ2=makeQuery(id+"F0.imprint","INTERSECT",VERTEX,{"disambiguationData":[OD(0.0)],"derivedFrom":[subQ1,subQ0]});Q8=makeQuery(id+"F0.imprint","IMPRINT",FACE,{"disambiguationData":[TD([[makeQuery(id+"F0.imprint","IMPRINT",EDGE,{"disambiguationData":[TD([[subQ2,-1.0]])],"derivedFrom":subQ1}),-1.0]])]});}
            var Q9;
            {var subQ0=sQuery(id+"F0.wireOp",EDGE,"E9");var subQ1=sQuery(id+"F0.wireOp",EDGE,"E0");var subQ2=makeQuery(id+"F0.imprint","INTERSECT",VERTEX,{"disambiguationData":[OD(0.0)],"derivedFrom":[subQ1,subQ0]});Q9=makeQuery(id+"F0.imprint","IMPRINT",FACE,{"disambiguationData":[TD([[makeQuery(id+"F0.imprint","IMPRINT",EDGE,{"disambiguationData":[TD([[subQ2,-1.0]])],"derivedFrom":subQ1}),-1.0]])]});}
            var Q10;
            {var subQ0=sQuery(id+"F0.wireOp",EDGE,"E9");var subQ1=sQuery(id+"F0.wireOp",EDGE,"E0");var subQ2=makeQuery(id+"F0.imprint","INTERSECT",VERTEX,{"disambiguationData":[OD(0.0)],"derivedFrom":[subQ1,subQ0]});Q10=makeQuery(id+"F0.imprint","IMPRINT",FACE,{"disambiguationData":[TD([[makeQuery(id+"F0.imprint","IMPRINT",EDGE,{"disambiguationData":[TD([[subQ2,-1.0]])],"derivedFrom":subQ1}),1.0]])]});}
            var Q11;
            {var subQ0=sQuery(id+"F0.wireOp",EDGE,"E23.0");var subQ1=sQuery(id+"F0.wireOp",EDGE,"E0");var subQ2=makeQuery(id+"F0.imprint","INTERSECT",VERTEX,{"disambiguationData":[OD(0.0)],"derivedFrom":[subQ1,subQ0]});Q11=makeQuery(id+"F0.imprint","IMPRINT",FACE,{"disambiguationData":[TD([[makeQuery(id+"F0.imprint","IMPRINT",EDGE,{"disambiguationData":[TD([[subQ2,-1.0]])],"derivedFrom":subQ1}),1.0]])]});}
            var Q12;
            {var subQ0=sQuery(id+"F0.wireOp",EDGE,"E22.0");var subQ1=sQuery(id+"F0.wireOp",EDGE,"E0");var subQ2=makeQuery(id+"F0.imprint","INTERSECT",VERTEX,{"disambiguationData":[OD(0.0)],"derivedFrom":[subQ1,subQ0]});Q12=makeQuery(id+"F0.imprint","IMPRINT",FACE,{"disambiguationData":[TD([[makeQuery(id+"F0.imprint","IMPRINT",EDGE,{"disambiguationData":[TD([[subQ2,-1.0]])],"derivedFrom":subQ1}),-1.0]])]});}
            var Q13;
            {var subQ0=sQuery(id+"F0.wireOp",EDGE,"E10");var subQ1=sQuery(id+"F0.wireOp",EDGE,"E0");var subQ2=makeQuery(id+"F0.imprint","INTERSECT",VERTEX,{"disambiguationData":[OD(0.0)],"derivedFrom":[subQ1,subQ0]});Q13=makeQuery(id+"F0.imprint","IMPRINT",FACE,{"disambiguationData":[TD([[makeQuery(id+"F0.imprint","IMPRINT",EDGE,{"disambiguationData":[TD([[subQ2,-1.0]])],"derivedFrom":subQ1}),-1.0]])]});}
            var Q14;
            {var subQ0=sQuery(id+"F0.wireOp",EDGE,"E10");var subQ1=sQuery(id+"F0.wireOp",EDGE,"E0");var subQ2=makeQuery(id+"F0.imprint","INTERSECT",VERTEX,{"disambiguationData":[OD(0.0)],"derivedFrom":[subQ1,subQ0]});Q14=makeQuery(id+"F0.imprint","IMPRINT",FACE,{"disambiguationData":[TD([[makeQuery(id+"F0.imprint","IMPRINT",EDGE,{"disambiguationData":[TD([[subQ2,-1.0]])],"derivedFrom":subQ1}),1.0]])]});}
            var Q15;
            {var subQ0=sQuery(id+"F0.wireOp",EDGE,"E22.0");var subQ1=sQuery(id+"F0.wireOp",EDGE,"E0");var subQ2=makeQuery(id+"F0.imprint","INTERSECT",VERTEX,{"disambiguationData":[OD(1.0)],"derivedFrom":[subQ1,subQ0]});Q15=makeQuery(id+"F0.imprint","IMPRINT",FACE,{"disambiguationData":[TD([[makeQuery(id+"F0.imprint","IMPRINT",EDGE,{"disambiguationData":[TD([[subQ2,1.0]])],"derivedFrom":subQ1}),1.0]])]});}
            var Q16;
            {var subQ0=sQuery(id+"F0.wireOp",EDGE,"E22.0");var subQ1=sQuery(id+"F0.wireOp",EDGE,"E0");var subQ2=makeQuery(id+"F0.imprint","INTERSECT",VERTEX,{"disambiguationData":[OD(0.0)],"derivedFrom":[subQ1,subQ0]});Q16=makeQuery(id+"F0.imprint","IMPRINT",FACE,{"disambiguationData":[TD([[makeQuery(id+"F0.imprint","IMPRINT",EDGE,{"disambiguationData":[TD([[subQ2,-1.0]])],"derivedFrom":subQ1}),1.0]])]});}
            var Q17;
            {var subQ0=sQuery(id+"F0.wireOp",EDGE,"E11.0");var subQ1=sQuery(id+"F0.wireOp",EDGE,"E0");var subQ2=makeQuery(id+"F0.imprint","INTERSECT",VERTEX,{"disambiguationData":[OD(0.0)],"derivedFrom":[subQ1,subQ0]});Q17=makeQuery(id+"F0.imprint","IMPRINT",FACE,{"disambiguationData":[TD([[makeQuery(id+"F0.imprint","IMPRINT",EDGE,{"disambiguationData":[TD([[subQ2,-1.0]])],"derivedFrom":subQ1}),-1.0]])]});}
            var Q18;
            {var subQ0=sQuery(id+"F0.wireOp",EDGE,"E4");var subQ1=sQuery(id+"F0.wireOp",EDGE,"E0");var subQ2=makeQuery(id+"F0.imprint","INTERSECT",VERTEX,{"disambiguationData":[OD(0.0)],"derivedFrom":[subQ1,subQ0]});Q18=makeQuery(id+"F0.imprint","IMPRINT",FACE,{"disambiguationData":[TD([[makeQuery(id+"F0.imprint","IMPRINT",EDGE,{"disambiguationData":[TD([[subQ2,-1.0]])],"derivedFrom":subQ1}),-1.0]])]});}
            var Q19;
            {var subQ0=sQuery(id+"F0.wireOp",EDGE,"E4");var subQ1=sQuery(id+"F0.wireOp",EDGE,"E0");var subQ2=makeQuery(id+"F0.imprint","INTERSECT",VERTEX,{"disambiguationData":[OD(0.0)],"derivedFrom":[subQ1,subQ0]});Q19=makeQuery(id+"F0.imprint","IMPRINT",FACE,{"disambiguationData":[TD([[makeQuery(id+"F0.imprint","IMPRINT",EDGE,{"disambiguationData":[TD([[subQ2,-1.0]])],"derivedFrom":subQ1}),1.0]])]});}
            var Q20;
            {var subQ0=sQuery(id+"F0.wireOp",EDGE,"E11.0");var subQ1=sQuery(id+"F0.wireOp",EDGE,"E0");var subQ2=makeQuery(id+"F0.imprint","INTERSECT",VERTEX,{"disambiguationData":[OD(0.0)],"derivedFrom":[subQ1,subQ0]});Q20=makeQuery(id+"F0.imprint","IMPRINT",FACE,{"disambiguationData":[TD([[makeQuery(id+"F0.imprint","IMPRINT",EDGE,{"disambiguationData":[TD([[subQ2,-1.0]])],"derivedFrom":subQ1}),1.0]])]});}
            var Q21;
            {var subQ0=sQuery(id+"F0.wireOp",EDGE,"E12.0");var subQ1=sQuery(id+"F0.wireOp",EDGE,"E0");var subQ2=makeQuery(id+"F0.imprint","INTERSECT",VERTEX,{"disambiguationData":[OD(0.0)],"derivedFrom":[subQ1,subQ0]});Q21=makeQuery(id+"F0.imprint","IMPRINT",FACE,{"disambiguationData":[TD([[makeQuery(id+"F0.imprint","IMPRINT",EDGE,{"disambiguationData":[TD([[subQ2,1.0]])],"derivedFrom":subQ1}),-1.0]])]});}
            var Q22;
            {var subQ0=sQuery(id+"F0.wireOp",EDGE,"E5");var subQ1=sQuery(id+"F0.wireOp",EDGE,"E0");var subQ2=makeQuery(id+"F0.imprint","INTERSECT",VERTEX,{"disambiguationData":[OD(0.0)],"derivedFrom":[subQ1,subQ0]});Q22=makeQuery(id+"F0.imprint","IMPRINT",FACE,{"disambiguationData":[TD([[makeQuery(id+"F0.imprint","IMPRINT",EDGE,{"disambiguationData":[TD([[subQ2,1.0]])],"derivedFrom":subQ1}),-1.0]])]});}
            var Q23;
            {var subQ0=sQuery(id+"F0.wireOp",EDGE,"E5");var subQ1=sQuery(id+"F0.wireOp",EDGE,"E0");var subQ2=makeQuery(id+"F0.imprint","INTERSECT",VERTEX,{"disambiguationData":[OD(0.0)],"derivedFrom":[subQ1,subQ0]});Q23=makeQuery(id+"F0.imprint","IMPRINT",FACE,{"disambiguationData":[TD([[makeQuery(id+"F0.imprint","IMPRINT",EDGE,{"disambiguationData":[TD([[subQ2,1.0]])],"derivedFrom":subQ1}),1.0]])]});}
            var Q24;
            {var subQ0=sQuery(id+"F0.wireOp",EDGE,"E12.0");var subQ1=sQuery(id+"F0.wireOp",EDGE,"E0");var subQ2=makeQuery(id+"F0.imprint","INTERSECT",VERTEX,{"disambiguationData":[OD(0.0)],"derivedFrom":[subQ1,subQ0]});Q24=makeQuery(id+"F0.imprint","IMPRINT",FACE,{"disambiguationData":[TD([[makeQuery(id+"F0.imprint","IMPRINT",EDGE,{"disambiguationData":[TD([[subQ2,1.0]])],"derivedFrom":subQ1}),1.0]])]});}
            var Q25;
            {var subQ0=sQuery(id+"F0.wireOp",EDGE,"E13.0");var subQ1=sQuery(id+"F0.wireOp",EDGE,"E0");var subQ2=makeQuery(id+"F0.imprint","INTERSECT",VERTEX,{"disambiguationData":[OD(0.0)],"derivedFrom":[subQ1,subQ0]});Q25=makeQuery(id+"F0.imprint","IMPRINT",FACE,{"disambiguationData":[TD([[makeQuery(id+"F0.imprint","IMPRINT",EDGE,{"disambiguationData":[TD([[subQ2,-1.0]])],"derivedFrom":subQ1}),-1.0]])]});}
            var Q26;
            {var subQ0=sQuery(id+"F0.wireOp",EDGE,"E6");var subQ1=sQuery(id+"F0.wireOp",EDGE,"E0");var subQ2=makeQuery(id+"F0.imprint","INTERSECT",VERTEX,{"disambiguationData":[OD(0.0)],"derivedFrom":[subQ1,subQ0]});Q26=makeQuery(id+"F0.imprint","IMPRINT",FACE,{"disambiguationData":[TD([[makeQuery(id+"F0.imprint","IMPRINT",EDGE,{"disambiguationData":[TD([[subQ2,-1.0]])],"derivedFrom":subQ1}),-1.0]])]});}
            var Q27;
            {var subQ0=sQuery(id+"F0.wireOp",EDGE,"E6");var subQ1=sQuery(id+"F0.wireOp",EDGE,"E0");var subQ2=makeQuery(id+"F0.imprint","INTERSECT",VERTEX,{"disambiguationData":[OD(0.0)],"derivedFrom":[subQ1,subQ0]});Q27=makeQuery(id+"F0.imprint","IMPRINT",FACE,{"disambiguationData":[TD([[makeQuery(id+"F0.imprint","IMPRINT",EDGE,{"disambiguationData":[TD([[subQ2,-1.0]])],"derivedFrom":subQ1}),1.0]])]});}
            var Q28;
            {var subQ0=sQuery(id+"F0.wireOp",EDGE,"E13.0");var subQ1=sQuery(id+"F0.wireOp",EDGE,"E0");var subQ2=makeQuery(id+"F0.imprint","INTERSECT",VERTEX,{"disambiguationData":[OD(0.0)],"derivedFrom":[subQ1,subQ0]});Q28=makeQuery(id+"F0.imprint","IMPRINT",FACE,{"disambiguationData":[TD([[makeQuery(id+"F0.imprint","IMPRINT",EDGE,{"disambiguationData":[TD([[subQ2,-1.0]])],"derivedFrom":subQ1}),1.0]])]});}
            extrude(context, id + "F3", {"entities" : qUnion([Q0, Q1, Q2, Q3, Q4, Q5, Q6, Q7, Q8, Q9, Q10, Q11, Q12, Q13, Q14, Q15, Q16, Q17, Q18, Q19, Q20, Q21, Q22, Q23, Q24, Q25, Q26, Q27, Q28]), "oppositeDirection" : true, "depth" : 20 * mm, "offsetDistance" : 25 * mm});
        }
        {
            var Q0;
            {var subQ0=sQuery(id+"F0.wireOp",EDGE,"E10");var subQ1=sQuery(id+"F0.wireOp",EDGE,"E0");var subQ2=makeQuery(id+"F0.imprint","INTERSECT",VERTEX,{"disambiguationData":[OD(0.0)],"derivedFrom":[subQ1,subQ0]});Q0=makeQuery(id+"F0.imprint","IMPRINT",FACE,{"disambiguationData":[TD([[makeQuery(id+"F0.imprint","IMPRINT",EDGE,{"disambiguationData":[TD([[subQ2,-1.0]])],"derivedFrom":subQ1}),-1.0]])]});}
            var Q1;
            {var subQ0=sQuery(id+"F0.wireOp",EDGE,"E10");var subQ1=sQuery(id+"F0.wireOp",EDGE,"E0");var subQ2=makeQuery(id+"F0.imprint","INTERSECT",VERTEX,{"disambiguationData":[OD(0.0)],"derivedFrom":[subQ1,subQ0]});Q1=makeQuery(id+"F0.imprint","IMPRINT",FACE,{"disambiguationData":[TD([[makeQuery(id+"F0.imprint","IMPRINT",EDGE,{"disambiguationData":[TD([[subQ2,-1.0]])],"derivedFrom":subQ1}),1.0]])]});}
            var Q2;
            {var subQ0=sQuery(id+"F0.wireOp",EDGE,"E4");var subQ1=sQuery(id+"F0.wireOp",EDGE,"E0");var subQ2=makeQuery(id+"F0.imprint","INTERSECT",VERTEX,{"disambiguationData":[OD(0.0)],"derivedFrom":[subQ1,subQ0]});Q2=makeQuery(id+"F0.imprint","IMPRINT",FACE,{"disambiguationData":[TD([[makeQuery(id+"F0.imprint","IMPRINT",EDGE,{"disambiguationData":[TD([[subQ2,-1.0]])],"derivedFrom":subQ1}),1.0]])]});}
            var Q3;
            {var subQ0=sQuery(id+"F0.wireOp",EDGE,"E4");var subQ1=sQuery(id+"F0.wireOp",EDGE,"E0");var subQ2=makeQuery(id+"F0.imprint","INTERSECT",VERTEX,{"disambiguationData":[OD(0.0)],"derivedFrom":[subQ1,subQ0]});Q3=makeQuery(id+"F0.imprint","IMPRINT",FACE,{"disambiguationData":[TD([[makeQuery(id+"F0.imprint","IMPRINT",EDGE,{"disambiguationData":[TD([[subQ2,-1.0]])],"derivedFrom":subQ1}),-1.0]])]});}
            var Q4;
            {var subQ0=sQuery(id+"F0.wireOp",EDGE,"E5");var subQ1=sQuery(id+"F0.wireOp",EDGE,"E0");var subQ2=makeQuery(id+"F0.imprint","INTERSECT",VERTEX,{"disambiguationData":[OD(0.0)],"derivedFrom":[subQ1,subQ0]});Q4=makeQuery(id+"F0.imprint","IMPRINT",FACE,{"disambiguationData":[TD([[makeQuery(id+"F0.imprint","IMPRINT",EDGE,{"disambiguationData":[TD([[subQ2,1.0]])],"derivedFrom":subQ1}),-1.0]])]});}
            var Q5;
            {var subQ0=sQuery(id+"F0.wireOp",EDGE,"E5");var subQ1=sQuery(id+"F0.wireOp",EDGE,"E0");var subQ2=makeQuery(id+"F0.imprint","INTERSECT",VERTEX,{"disambiguationData":[OD(0.0)],"derivedFrom":[subQ1,subQ0]});Q5=makeQuery(id+"F0.imprint","IMPRINT",FACE,{"disambiguationData":[TD([[makeQuery(id+"F0.imprint","IMPRINT",EDGE,{"disambiguationData":[TD([[subQ2,1.0]])],"derivedFrom":subQ1}),1.0]])]});}
            var Q6;
            {var subQ0=sQuery(id+"F0.wireOp",EDGE,"E6");var subQ1=sQuery(id+"F0.wireOp",EDGE,"E0");var subQ2=makeQuery(id+"F0.imprint","INTERSECT",VERTEX,{"disambiguationData":[OD(0.0)],"derivedFrom":[subQ1,subQ0]});Q6=makeQuery(id+"F0.imprint","IMPRINT",FACE,{"disambiguationData":[TD([[makeQuery(id+"F0.imprint","IMPRINT",EDGE,{"disambiguationData":[TD([[subQ2,-1.0]])],"derivedFrom":subQ1}),-1.0]])]});}
            var Q7;
            {var subQ0=sQuery(id+"F0.wireOp",EDGE,"E6");var subQ1=sQuery(id+"F0.wireOp",EDGE,"E0");var subQ2=makeQuery(id+"F0.imprint","INTERSECT",VERTEX,{"disambiguationData":[OD(0.0)],"derivedFrom":[subQ1,subQ0]});Q7=makeQuery(id+"F0.imprint","IMPRINT",FACE,{"disambiguationData":[TD([[makeQuery(id+"F0.imprint","IMPRINT",EDGE,{"disambiguationData":[TD([[subQ2,-1.0]])],"derivedFrom":subQ1}),1.0]])]});}
            var Q8;
            {var subQ0=sQuery(id+"F0.wireOp",EDGE,"E7");var subQ1=sQuery(id+"F0.wireOp",EDGE,"E0");var subQ2=makeQuery(id+"F0.imprint","INTERSECT",VERTEX,{"disambiguationData":[OD(0.0)],"derivedFrom":[subQ1,subQ0]});Q8=makeQuery(id+"F0.imprint","IMPRINT",FACE,{"disambiguationData":[TD([[makeQuery(id+"F0.imprint","IMPRINT",EDGE,{"disambiguationData":[TD([[subQ2,-1.0]])],"derivedFrom":subQ1}),-1.0]])]});}
            var Q9;
            {var subQ0=sQuery(id+"F0.wireOp",EDGE,"E7");var subQ1=sQuery(id+"F0.wireOp",EDGE,"E0");var subQ2=makeQuery(id+"F0.imprint","INTERSECT",VERTEX,{"disambiguationData":[OD(0.0)],"derivedFrom":[subQ1,subQ0]});Q9=makeQuery(id+"F0.imprint","IMPRINT",FACE,{"disambiguationData":[TD([[makeQuery(id+"F0.imprint","IMPRINT",EDGE,{"disambiguationData":[TD([[subQ2,-1.0]])],"derivedFrom":subQ1}),1.0]])]});}
            var Q10;
            {var subQ0=sQuery(id+"F0.wireOp",EDGE,"E8");var subQ1=sQuery(id+"F0.wireOp",EDGE,"E0");var subQ2=makeQuery(id+"F0.imprint","INTERSECT",VERTEX,{"disambiguationData":[OD(0.0)],"derivedFrom":[subQ1,subQ0]});Q10=makeQuery(id+"F0.imprint","IMPRINT",FACE,{"disambiguationData":[TD([[makeQuery(id+"F0.imprint","IMPRINT",EDGE,{"disambiguationData":[TD([[subQ2,-1.0]])],"derivedFrom":subQ1}),-1.0]])]});}
            var Q11;
            {var subQ0=sQuery(id+"F0.wireOp",EDGE,"E8");var subQ1=sQuery(id+"F0.wireOp",EDGE,"E0");var subQ2=makeQuery(id+"F0.imprint","INTERSECT",VERTEX,{"disambiguationData":[OD(0.0)],"derivedFrom":[subQ1,subQ0]});Q11=makeQuery(id+"F0.imprint","IMPRINT",FACE,{"disambiguationData":[TD([[makeQuery(id+"F0.imprint","IMPRINT",EDGE,{"disambiguationData":[TD([[subQ2,-1.0]])],"derivedFrom":subQ1}),1.0]])]});}
            var Q12;
            {var subQ0=sQuery(id+"F0.wireOp",EDGE,"E9");var subQ1=sQuery(id+"F0.wireOp",EDGE,"E0");var subQ2=makeQuery(id+"F0.imprint","INTERSECT",VERTEX,{"disambiguationData":[OD(0.0)],"derivedFrom":[subQ1,subQ0]});Q12=makeQuery(id+"F0.imprint","IMPRINT",FACE,{"disambiguationData":[TD([[makeQuery(id+"F0.imprint","IMPRINT",EDGE,{"disambiguationData":[TD([[subQ2,-1.0]])],"derivedFrom":subQ1}),-1.0]])]});}
            var Q13;
            {var subQ0=sQuery(id+"F0.wireOp",EDGE,"E9");var subQ1=sQuery(id+"F0.wireOp",EDGE,"E0");var subQ2=makeQuery(id+"F0.imprint","INTERSECT",VERTEX,{"disambiguationData":[OD(0.0)],"derivedFrom":[subQ1,subQ0]});Q13=makeQuery(id+"F0.imprint","IMPRINT",FACE,{"disambiguationData":[TD([[makeQuery(id+"F0.imprint","IMPRINT",EDGE,{"disambiguationData":[TD([[subQ2,-1.0]])],"derivedFrom":subQ1}),1.0]])]});}
            extrude(context, id + "F4", {"entities" : qUnion([Q0, Q1, Q2, Q3, Q4, Q5, Q6, Q7, Q8, Q9, Q10, Q11, Q12, Q13]), "operationType" : NewBodyOperationType.REMOVE, "oppositeDirection" : true, "depth" : 18 * mm, "offsetDistance" : 25 * mm});
        }
        {
            var Q0;
            Q0=makeQuery(id+"F1.opExtrude","CAP_FACE",FACE,{"disambiguationData":[OSD([sQuery(id+"F0.wireOp",EDGE,"E0"),sQuery(id+"F0.wireOp",EDGE,"E16.0"),sQuery(id+"F0.wireOp",EDGE,"E17.0"),sQuery(id+"F0.wireOp",EDGE,"E18.0"),sQuery(id+"F0.wireOp",EDGE,"E19.0"),sQuery(id+"F0.wireOp",EDGE,"E20.0"),sQuery(id+"F0.wireOp",EDGE,"E21.0"),sQuery(id+"F0.wireOp",EDGE,"E24.0")])],"isStart":true});
            var sketch = newSketch(context, id + "F5", { "sketchPlane" : qUnion([Q0])});
            skCircle(sketch, "E25", {"center": v(0, 0) * mm, "radius": 6.25 * mm});
            skSolve(sketch);
        }
        {
            var Q0;
            Q0=makeQuery(id+"F5.imprint","IMPRINT",FACE,{"disambiguationData":[TD([[makeQuery(id+"F5.imprint","IMPRINT",EDGE,{"derivedFrom":sQuery(id+"F5.wireOp",EDGE,"E25")}),1.0]])]});
            extrude(context, id + "F6", {"entities" : qUnion([Q0]), "operationType" : NewBodyOperationType.ADD, "depth" : 6 * mm, "offsetDistance" : 25 * mm});
        }
        {
            var Q0;
            Q0=makeQuery(id+"F1.opExtrude","CAP_FACE",FACE,{"disambiguationData":[OSD([sQuery(id+"F0.wireOp",EDGE,"E0"),sQuery(id+"F0.wireOp",EDGE,"E16.0"),sQuery(id+"F0.wireOp",EDGE,"E17.0"),sQuery(id+"F0.wireOp",EDGE,"E18.0"),sQuery(id+"F0.wireOp",EDGE,"E19.0"),sQuery(id+"F0.wireOp",EDGE,"E20.0"),sQuery(id+"F0.wireOp",EDGE,"E21.0"),sQuery(id+"F0.wireOp",EDGE,"E24.0")])],"isStart":true});
            var sketch = newSketch(context, id + "F7", { "sketchPlane" : qUnion([Q0])});
            skCircle(sketch, "E26", {"center": v(0, 0) * mm, "radius": 66.25 * mm});
            skCircle(sketch, "E27", {"center": v(0, 0) * mm, "radius": 6.5 * mm});
            skSolve(sketch);
        }
        {
            var Q0;
            Q0=makeQuery(id+"F7.imprint","IMPRINT",FACE,{"disambiguationData":[TD([[makeQuery(id+"F7.imprint","IMPRINT",EDGE,{"derivedFrom":sQuery(id+"F7.wireOp",EDGE,"E26")}),1.0]])]});
            var Q1;
            Q1=makeQuery(id+"F7.imprint","IMPRINT",FACE,{"disambiguationData":[TD([[makeQuery(id+"F7.imprint","IMPRINT",EDGE,{"derivedFrom":sQuery(id+"F7.wireOp",EDGE,"E27")}),-1.0]])]});
            extrude(context, id + "F8", {"entities" : qUnion([Q0, Q1]), "depth" : 3 * mm, "offsetDistance" : 25 * mm});
        }
        {
            var Q0;
            Q0=makeQuery(id+"F8.opExtrude","CAP_FACE",FACE,{"disambiguationData":[OSD([sQuery(id+"F7.wireOp",EDGE,"E26"),sQuery(id+"F7.wireOp",EDGE,"E27")])],"isStart":false});
            var sketch = newSketch(context, id + "F9", { "sketchPlane" : qUnion([Q0])});
            skCircle(sketch, "E28", {"center": v(0, 0) * mm, "radius": 47.5 * mm});
            skLineSegment(sketch, "E29", {"start": v(0, 0) * mm, "end": v(0, 66.25) * mm});
            skArc(sketch, "E30", {"start": v(-2.6, 33.24) * mm, "mid": v(14.33, 49.71) * mm, "end": v(-6.79, 60.31) * mm});
            skArc(sketch, "E31", {"start": v(-18.9, 53.9) * mm, "mid": v(-23.97, 43.8) * mm, "end": v(-16.08, 35.7) * mm});
            skLineSegment(sketch, "E32", {"start": v(-6.79, 60.31) * mm, "end": v(-18.9, 53.9) * mm});
            skLineSegment(sketch, "E33", {"start": v(-16.08, 35.7) * mm, "end": v(-2.6, 33.24) * mm});
            skLineSegment(sketch, "E34.1.0", {"start": v(43.1, 42.73) * mm, "end": v(30.56, 48.25) * mm});
            skArc(sketch, "E34.1.1", {"start": v(24.46, 22.66) * mm, "mid": v(47.88, 19.6) * mm, "end": v(43.1, 42.73) * mm});
            skLineSegment(sketch, "E34.1.2", {"start": v(18.03, 34.75) * mm, "end": v(24.46, 22.66) * mm});
            skArc(sketch, "E34.1.3", {"start": v(30.56, 48.25) * mm, "mid": v(19.5, 45.96) * mm, "end": v(18.03, 34.75) * mm});
            skLineSegment(sketch, "E34.2.0", {"start": v(60.25, -7.3) * mm, "end": v(56.8, 5.95) * mm});
            skArc(sketch, "E34.2.1", {"start": v(32.94, -5.13) * mm, "mid": v(45.07, -25.4) * mm, "end": v(60.25, -7.3) * mm});
            skLineSegment(sketch, "E34.2.2", {"start": v(38.44, 7.42) * mm, "end": v(32.94, -5.13) * mm});
            skArc(sketch, "E34.2.3", {"start": v(56.8, 5.95) * mm, "mid": v(48.14, 13.22) * mm, "end": v(38.44, 7.42) * mm});
            skLineSegment(sketch, "E34.3.0", {"start": v(31.64, -51.8) * mm, "end": v(39.9, -40.87) * mm});
            skArc(sketch, "E34.3.1", {"start": v(16.4, -29.02) * mm, "mid": v(8.02, -51.11) * mm, "end": v(31.64, -51.8) * mm});
            skLineSegment(sketch, "E34.3.2", {"start": v(29.66, -25.55) * mm, "end": v(16.4, -29.02) * mm});
            skArc(sketch, "E34.3.3", {"start": v(39.9, -40.87) * mm, "mid": v(40.23, -29.57) * mm, "end": v(29.66, -25.55) * mm});
            skLineSegment(sketch, "E34.4.0", {"start": v(-21, -56.94) * mm, "end": v(-7.3, -56.65) * mm});
            skArc(sketch, "E34.4.1", {"start": v(-12.59, -30.87) * mm, "mid": v(-35.12, -38) * mm, "end": v(-21, -56.94) * mm});
            skLineSegment(sketch, "E34.4.2", {"start": v(-1.65, -39.12) * mm, "end": v(-12.59, -30.87) * mm});
            skArc(sketch, "E34.4.3", {"start": v(-7.3, -56.65) * mm, "mid": v(1.76, -49.9) * mm, "end": v(-1.65, -39.12) * mm});
            skLineSegment(sketch, "E34.5.0", {"start": v(-57.7, -18.84) * mm, "end": v(-48.97, -29.4) * mm});
            skArc(sketch, "E34.5.1", {"start": v(-32.02, -9.27) * mm, "mid": v(-51.58, 3.98) * mm, "end": v(-57.7, -18.84) * mm});
            skLineSegment(sketch, "E34.5.2", {"start": v(-31.7, -22.97) * mm, "end": v(-32.02, -9.27) * mm});
            skArc(sketch, "E34.5.3", {"start": v(-48.97, -29.4) * mm, "mid": v(-38.05, -32.33) * mm, "end": v(-31.7, -22.97) * mm});
            skLineSegment(sketch, "E34.6.0", {"start": v(-50.57, 33.57) * mm, "end": v(-53.44, 20.18) * mm});
            skArc(sketch, "E34.6.1", {"start": v(-27.13, 19.37) * mm, "mid": v(-28.87, 42.93) * mm, "end": v(-50.57, 33.57) * mm});
            skLineSegment(sketch, "E34.6.2", {"start": v(-37.68, 10.63) * mm, "end": v(-27.13, 19.37) * mm});
            skArc(sketch, "E34.6.3", {"start": v(-53.44, 20.18) * mm, "mid": v(-48.96, 9.8) * mm, "end": v(-37.68, 10.63) * mm});
            skLineSegment(sketch, "E34.anchor1", {"start": v(0, 0) * mm, "end": v(-18.9, 53.9) * mm, "construction": true});
            skLineSegment(sketch, "E34.anchor2", {"start": v(0, 0) * mm, "end": v(-53.44, 20.18) * mm, "construction": true});
            skSolve(sketch);
        }
        {
            var Q0;
            {var subQ5=sQuery(id+"F9.wireOp",EDGE,"E34.6.0");Q0=makeQuery(id+"F9.imprint","IMPRINT",FACE,{"disambiguationData":[TD([[makeQuery(id+"F9.imprint","IMPRINT",EDGE,{"derivedFrom":subQ5}),1.0]])]});}
            var Q1;
            {var subQ5=sQuery(id+"F9.wireOp",EDGE,"E34.6.2");Q1=makeQuery(id+"F9.imprint","IMPRINT",FACE,{"disambiguationData":[TD([[makeQuery(id+"F9.imprint","IMPRINT",EDGE,{"derivedFrom":subQ5}),1.0]])]});}
            var Q2;
            {var subQ0=sQuery(id+"F9.wireOp",EDGE,"E32");Q2=makeQuery(id+"F9.imprint","IMPRINT",FACE,{"disambiguationData":[TD([[makeQuery(id+"F9.imprint","IMPRINT",EDGE,{"derivedFrom":subQ0}),1.0]])]});}
            var Q3;
            {var subQ0=sQuery(id+"F9.wireOp",EDGE,"E30");var subQ1=sQuery(id+"F9.wireOp",EDGE,"E28");var subQ2=makeQuery(id+"F9.imprint","INTERSECT",VERTEX,{"derivedFrom":[subQ1,subQ0]});Q3=makeQuery(id+"F9.imprint","IMPRINT",FACE,{"disambiguationData":[TD([[makeQuery(id+"F9.imprint","IMPRINT",EDGE,{"disambiguationData":[TD([[subQ2,-1.0]])],"derivedFrom":subQ1}),-1.0]])]});}
            var Q4;
            {var subQ0=sQuery(id+"F9.wireOp",EDGE,"E30");var subQ1=sQuery(id+"F9.wireOp",EDGE,"E28");var subQ2=makeQuery(id+"F9.imprint","INTERSECT",VERTEX,{"derivedFrom":[subQ1,subQ0]});Q4=makeQuery(id+"F9.imprint","IMPRINT",FACE,{"disambiguationData":[TD([[makeQuery(id+"F9.imprint","IMPRINT",EDGE,{"disambiguationData":[TD([[subQ2,-1.0]])],"derivedFrom":subQ1}),1.0]])]});}
            var Q5;
            {var subQ0=sQuery(id+"F9.wireOp",EDGE,"E33");Q5=makeQuery(id+"F9.imprint","IMPRINT",FACE,{"disambiguationData":[TD([[makeQuery(id+"F9.imprint","IMPRINT",EDGE,{"derivedFrom":subQ0}),1.0]])]});}
            var Q6;
            {var subQ5=sQuery(id+"F9.wireOp",EDGE,"E34.1.0");Q6=makeQuery(id+"F9.imprint","IMPRINT",FACE,{"disambiguationData":[TD([[makeQuery(id+"F9.imprint","IMPRINT",EDGE,{"derivedFrom":subQ5}),1.0]])]});}
            var Q7;
            {var subQ5=sQuery(id+"F9.wireOp",EDGE,"E34.1.2");Q7=makeQuery(id+"F9.imprint","IMPRINT",FACE,{"disambiguationData":[TD([[makeQuery(id+"F9.imprint","IMPRINT",EDGE,{"derivedFrom":subQ5}),1.0]])]});}
            var Q8;
            {var subQ5=sQuery(id+"F9.wireOp",EDGE,"E34.2.0");Q8=makeQuery(id+"F9.imprint","IMPRINT",FACE,{"disambiguationData":[TD([[makeQuery(id+"F9.imprint","IMPRINT",EDGE,{"derivedFrom":subQ5}),1.0]])]});}
            var Q9;
            {var subQ5=sQuery(id+"F9.wireOp",EDGE,"E34.2.2");Q9=makeQuery(id+"F9.imprint","IMPRINT",FACE,{"disambiguationData":[TD([[makeQuery(id+"F9.imprint","IMPRINT",EDGE,{"derivedFrom":subQ5}),1.0]])]});}
            var Q10;
            {var subQ5=sQuery(id+"F9.wireOp",EDGE,"E34.3.0");Q10=makeQuery(id+"F9.imprint","IMPRINT",FACE,{"disambiguationData":[TD([[makeQuery(id+"F9.imprint","IMPRINT",EDGE,{"derivedFrom":subQ5}),1.0]])]});}
            var Q11;
            {var subQ5=sQuery(id+"F9.wireOp",EDGE,"E34.3.2");Q11=makeQuery(id+"F9.imprint","IMPRINT",FACE,{"disambiguationData":[TD([[makeQuery(id+"F9.imprint","IMPRINT",EDGE,{"derivedFrom":subQ5}),1.0]])]});}
            var Q12;
            {var subQ5=sQuery(id+"F9.wireOp",EDGE,"E34.4.0");Q12=makeQuery(id+"F9.imprint","IMPRINT",FACE,{"disambiguationData":[TD([[makeQuery(id+"F9.imprint","IMPRINT",EDGE,{"derivedFrom":subQ5}),1.0]])]});}
            var Q13;
            {var subQ5=sQuery(id+"F9.wireOp",EDGE,"E34.4.2");Q13=makeQuery(id+"F9.imprint","IMPRINT",FACE,{"disambiguationData":[TD([[makeQuery(id+"F9.imprint","IMPRINT",EDGE,{"derivedFrom":subQ5}),1.0]])]});}
            var Q14;
            {var subQ5=sQuery(id+"F9.wireOp",EDGE,"E34.5.0");Q14=makeQuery(id+"F9.imprint","IMPRINT",FACE,{"disambiguationData":[TD([[makeQuery(id+"F9.imprint","IMPRINT",EDGE,{"derivedFrom":subQ5}),1.0]])]});}
            var Q15;
            {var subQ5=sQuery(id+"F9.wireOp",EDGE,"E34.5.2");Q15=makeQuery(id+"F9.imprint","IMPRINT",FACE,{"disambiguationData":[TD([[makeQuery(id+"F9.imprint","IMPRINT",EDGE,{"derivedFrom":subQ5}),1.0]])]});}
            extrude(context, id + "F10", {"entities" : qUnion([Q0, Q1, Q2, Q3, Q4, Q5, Q6, Q7, Q8, Q9, Q10, Q11, Q12, Q13, Q14, Q15]), "operationType" : NewBodyOperationType.REMOVE, "endBound" : BoundingType.UP_TO_NEXT, "oppositeDirection" : true, "depth" : 25 * mm, "offsetDistance" : 25 * mm});
        }
        {
            var Q0;
            Q0=makeQuery(id+"F8.opExtrude","CAP_FACE",FACE,{"disambiguationData":[OSD([sQuery(id+"F7.wireOp",EDGE,"E26"),sQuery(id+"F7.wireOp",EDGE,"E27")])],"isStart":false});
            var sketch = newSketch(context, id + "F11", { "sketchPlane" : qUnion([Q0])});
            skLineSegment(sketch, "E35.bottom", {"start": v(7.25, 7.25) * mm, "end": v(-7.25, 7.25) * mm});
            skLineSegment(sketch, "E35.top", {"start": v(7.25, -7.25) * mm, "end": v(-7.25, -7.25) * mm});
            skLineSegment(sketch, "E35.left", {"start": v(7.25, 7.25) * mm, "end": v(7.25, -7.25) * mm});
            skLineSegment(sketch, "E35.right", {"start": v(-7.25, 7.25) * mm, "end": v(-7.25, -7.25) * mm});
            skPoint(sketch, "E35.middle", {"position": v(0, 0) * mm});
            skCircle(sketch, "E36", {"center": v(0, 0) * mm, "radius": 6.5 * mm});
            skSolve(sketch);
        }
        {
            var Q0;
            Q0=makeQuery(id+"F11.imprint","IMPRINT",FACE,{"disambiguationData":[TD([[makeQuery(id+"F11.imprint","IMPRINT",EDGE,{"derivedFrom":sQuery(id+"F11.wireOp",EDGE,"E35.bottom")}),1.0]])]});
            extrude(context, id + "F12", {"entities" : qUnion([Q0]), "operationType" : NewBodyOperationType.ADD, "depth" : 3 * mm, "offsetDistance" : 25 * mm});
        }
        {
            var Q0;
            Q0=makeQuery(id+"F8.opExtrude","SWEPT_BODY",BODY,{"disambiguationData":[OSD([sQuery(id+"F7.wireOp",EDGE,"E26"),sQuery(id+"F7.wireOp",EDGE,"E27")])]});
            transform(context, id + "F13", {"entities" : qUnion([Q0]), "transformType" : TransformType.TRANSLATION_3D, "dx" : 0 * mm, "dy" : 0 * mm, "dz" : 0 * mm, "makeCopy" : true});
        }
    });
